# Revit family: 84310180(2021)
name_source: partatom
category: Plumbing Fixtures
units: mm (PartAtom-declared; Revit-internal decimal feet)

## family parameters
Always vertical = Yes
Cut with Voids When Loaded = No
OmniClass Number = 23.45.55.00
OmniClass Title = Sanitary Faucets, Wastes
Part Type = Normal
Room Calculation Point = No
Round Connector Dimension = Use Diameter
Shared = No
Work Plane-Based = No

## types (1)
- 84310180 Hand shower, Bluetooth
    2D/3D/BIM Files URL = http://static.hansa.com
    3D View = https://static.hansa.com
    Additional Features = Display with real time feedback about the water and energy consumption
    AssetType = Fixed
    BIMObjectName = 84310180(2021)
    Bluetooth = 4.x (D054404)
    BodyMaterial = Brass
    Brand = HANSA
    Catalog Drawing URL = http://static.hansa.com
    Category = Shower solutions
    CloseOffRating = 0
    Color = Chrome/Light grey
    Connection Size = G1/2
    Default Elevation = 0 mm  [stored 0 ft]
    Dimension Drawing URL = http://static.hansa.com
    DurationUnit = Year
    EAN Number = 4057304015618
    EMC Directive = Radio Equipment Directive 2014/53/EU , 
Low Voltage Directive 2014/35/EU , 
EMC Directive 2014/30/EU , 
RoHS Directive 2011/65/EU
    EN Standard = EN 1112, ETSI EN 301 489-1 V1.9.2 , 
ETSI EN 300 328 v2.2.2 , 
EN 61000-6-1:2007 , 
EN 61000-6-3:2007+A1:2011+AC:2012 , 
EN 60335-1:2012+A11+A13+A1+A14+A2+A15:2021, Part 19.11.4
    ETIM Class Number = EC010161 Hand shower
    Electronic Parts = Light indicated function(s)
    FDV Document URL = http://www.hansa.com
    FaucetMainMaterial = Brass
    Features = Self-powered;Bluetooth®
    Finish = Polished
    Flow Drawing URL = http://static.hansa.com
    Flow Rate At 300kPa With Flow Controller = 0.2 L/s
    FlowCoefficient = 0
    Group = Hand shower
    Hand Shower Size = Ø 120 mm
    IfcExportAs = IfcValveType
    IfcExportType = FAUCET
    Installation and Maintenance Guide URL = http://static.hansa.com
    Interactive AR View URL = https://static.hansa.com
    Lifestyle photo = http://static.hansa.com
    Long Marketing = Digital hand shower
Designed to help you save water – with little effort.

Save up to 22% in water and energy consumption with our new HANSAACTIVEJET Digital hand shower. By connecting the hand shower to the Digital Hand Shower App, you can set water consumption goals, receive data on your long-term usage, and to access tips on saving water.

- Integrated display provides insights on total water and energy consumptions
- Powered by water flow – no batteries required
- Simple to attach – fits to all standard showers
    Manufacturer = HANSA
    ManufacturerName = HANSA
    ManufacturerURL = http://www.hansa.com
    Market = International;Germany;Austria;Switzerland;Belgium;Netherlands;France;Czech Republic;Slovakia;Hungary;Romania;Italy;Spain;Greece;Portugal;Australia
    Material = Composite
    Max. Hot Water Supply = 65 °C
    Mobile Product Information URL = http://mpi.hansa.com
    Model = 84310180 Hand shower, Bluetooth
    ModelReference = 84310180
    NBSDescription = Shower mixers
    NBSReference = 45-35-70/335
    Name = 84310180 Hand shower, Bluetooth
    Name_en = 84310180 Hand shower, Bluetooth
    NominalDepth = 65 mm
    NominalHeight = 266 mm
    NominalWidth = 118 mm
    Operating Voltage = 0 V
    PackageDimensions = 300.0 x 200.0 x 30.0
    Product Code = 84310180
    Product Family = HANSAACTIVEJET Digital
    Product Image URL = http://static.hansa.com
    Product URL = http://static.hansa.com
    Protection Class = IP X7
    Sales Package dimensions (LxWxH) = 277 x 125 x 79,5
    Shape = Sculptured
    Shower Parts = Anti limescale technology (easy to clean)
    Shower Spray = Sensitive
    Shower Spray Number = 1 shower spray
    Size = 120x65x265 mm
    Surface treatment = Chrome/Light grey
    Technical DataSheet URL = http://www.hansa.com
    UNSPSC Class Number = 30181803 Hand held shower unit
    URL Declaration Of Performance (DOP) = http://static.hansa.com
    URL Declaration of Asbestos = http://static.hansa.com
    URL Declaration of Conformity = http://static.hansa.com
    URL Declaration of SCIP = http://static.hansa.com
    URL EU Packaging Declaration = http://static.hansa.com
    URL EcoLabel Declaration = http://static.hansa.com
    URL Materials Declaration = http://www.hansa.com
    URL REACH = http://static.hansa.com
    URL UWL = http://static.hansa.com
    URL WEEE = http://static.hansa.com
    Uniclass2 = Pr_40_30_96_78
    Uniclass2015Description = Shower manual water supply sets
    Uniclass2015Reference = Pr_40_20_87_78
    Version = 1
    VersionDate = 01/06/2023
    Warranty Information URL = http://warranty.hansa.com
    WarrantyDescription = http://warranty.hansa.com
    WarrantyDurationUnit = Year
    Working Pressure = 50 - 500 kPa

note: [stored X ft] marks values corroborated as IEEE doubles in the binary element streams (Revit-internal decimal feet)

## geometry (parser evidence)
native form markers: Sweep x5
no freeform markers — native parametric forms only
